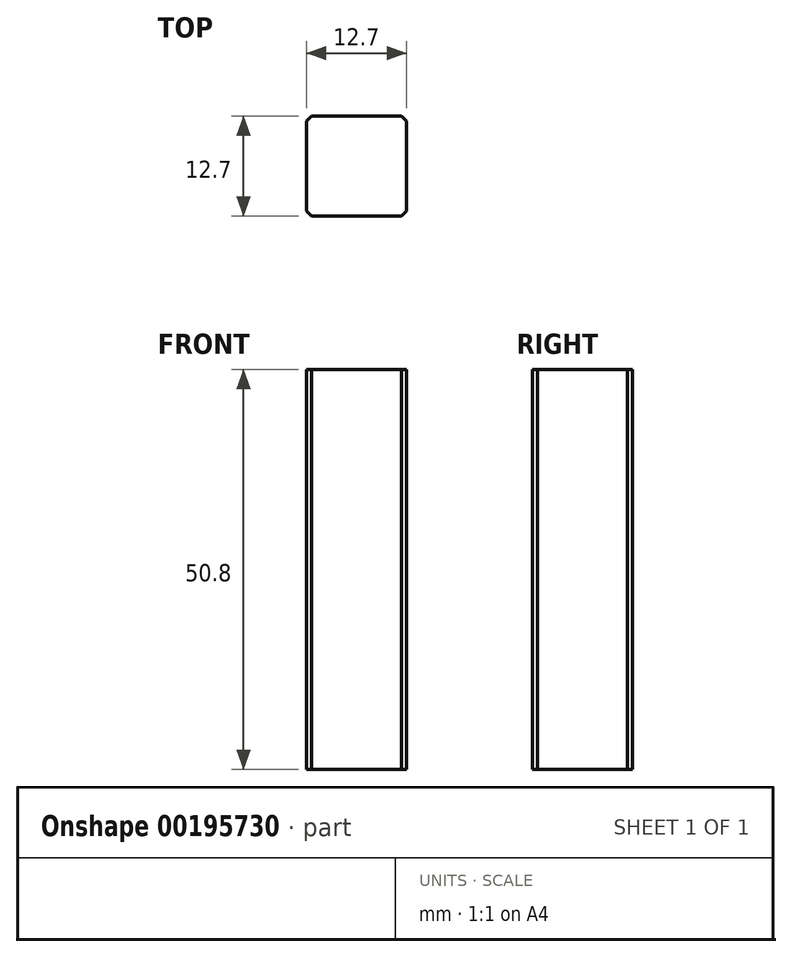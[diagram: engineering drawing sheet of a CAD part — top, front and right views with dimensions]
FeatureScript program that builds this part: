
annotation { "Feature Type Name" : "Feature", "Feature Type Description" : "" }
export const myFeature = defineFeature(function(context is Context, id is Id, definition is map)
    precondition{}
    {
        {
            var Q0;
            Q0=qCreatedBy(makeId("Top.planeOp"),FACE);
            var sketch = newSketch(context, id + "F0", { "sketchPlane" : qUnion([Q0])});
            skLineSegment(sketch, "E0.bottom", {"start": v(6.35, 6.35) * mm, "end": v(-6.35, 6.35) * mm});
            skLineSegment(sketch, "E0.top", {"start": v(6.35, -6.35) * mm, "end": v(-6.35, -6.35) * mm});
            skLineSegment(sketch, "E0.left", {"start": v(6.35, 6.35) * mm, "end": v(6.35, -6.35) * mm});
            skLineSegment(sketch, "E0.right", {"start": v(-6.35, 6.35) * mm, "end": v(-6.35, -6.35) * mm});
            skPoint(sketch, "E0.middle", {"position": v(0, 0) * mm});
            skSolve(sketch);
        }
        {
            var Q0;
            Q0 = qSketchRegion(id + "F0", true);
            extrude(context, id + "F1", {"entities" : qUnion([Q0]), "depth" : 50.8 * mm});
        }
        {
            var Q0;
            Q0=makeQuery(id+"F1.opExtrude","SWEPT_EDGE",EDGE,{"disambiguationData":[OSD([sQuery(id+"F0.wireOp",EDGE,"E0.bottom"),sQuery(id+"F0.wireOp",EDGE,"E0.right")])]});
            var Q1;
            Q1=makeQuery(id+"F1.opExtrude","SWEPT_EDGE",EDGE,{"disambiguationData":[OSD([sQuery(id+"F0.wireOp",EDGE,"E0.top"),sQuery(id+"F0.wireOp",EDGE,"E0.right")])]});
            var Q2;
            Q2=makeQuery(id+"F1.opExtrude","SWEPT_EDGE",EDGE,{"disambiguationData":[OSD([sQuery(id+"F0.wireOp",EDGE,"E0.bottom"),sQuery(id+"F0.wireOp",EDGE,"E0.left")])]});
            var Q3;
            Q3=makeQuery(id+"F1.opExtrude","SWEPT_EDGE",EDGE,{"disambiguationData":[OSD([sQuery(id+"F0.wireOp",EDGE,"E0.top"),sQuery(id+"F0.wireOp",EDGE,"E0.left")])]});
            chamfer(context, id + "F2", {"entities" : qUnion([Q0, Q1, Q2, Q3]), "width" : 0.64 * mm, "tangentPropagation" : true});
        }
    });
